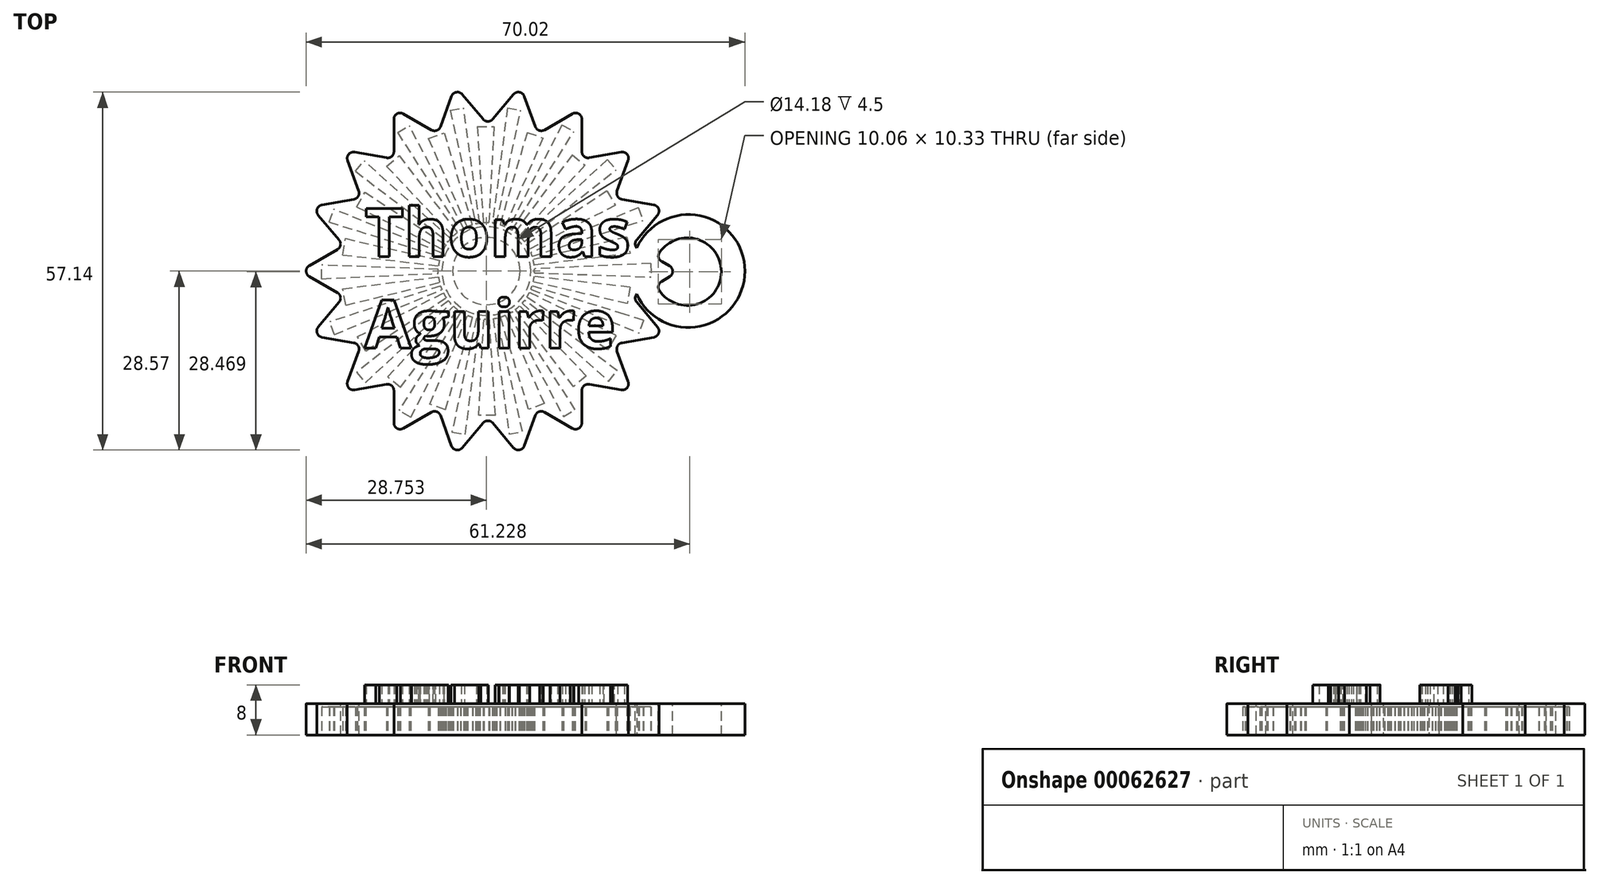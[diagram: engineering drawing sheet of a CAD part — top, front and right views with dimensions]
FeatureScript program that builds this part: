
annotation { "Feature Type Name" : "Feature", "Feature Type Description" : "" }
export const myFeature = defineFeature(function(context is Context, id is Id, definition is map)
    precondition{}
    {
        {
            var Q0;
            Q0=qCreatedBy(makeId("Top.planeOp"),FACE);
            var sketch = newSketch(context, id + "F0", { "sketchPlane" : qUnion([Q0])});
            skLineSegment(sketch, "E0", {"start": v(-64.22, 4.05) * mm, "end": v(-69.43, 10.26) * mm});
            skLineSegment(sketch, "E1", {"start": v(-69.43, 10.26) * mm, "end": v(-61.45, 11.67) * mm});
            skCircle(sketch, "E2.0", {"center": v(-41.24, 0) * mm, "radius": 30 * mm, "construction": true});
            skLineSegment(sketch, "E3", {"start": v(-61.45, 11.67) * mm, "end": v(-64.22, 19.28) * mm});
            skLineSegment(sketch, "E4", {"start": v(-64.22, 19.28) * mm, "end": v(-56.24, 17.88) * mm});
            skLineSegment(sketch, "E5", {"start": v(-56.24, 17.88) * mm, "end": v(-56.24, 25.98) * mm});
            skLineSegment(sketch, "E6", {"start": v(-56.24, 25.98) * mm, "end": v(-49.22, 21.93) * mm});
            skLineSegment(sketch, "E7", {"start": v(-49.22, 21.93) * mm, "end": v(-46.45, 29.54) * mm});
            skLineSegment(sketch, "E8", {"start": v(-46.45, 29.54) * mm, "end": v(-41.24, 23.34) * mm});
            skLineSegment(sketch, "E9", {"start": v(-41.24, 23.34) * mm, "end": v(-36.03, 29.54) * mm});
            skLineSegment(sketch, "E10", {"start": v(-36.03, 29.54) * mm, "end": v(-33.26, 21.93) * mm});
            skLineSegment(sketch, "E11", {"start": v(-33.26, 21.93) * mm, "end": v(-26.24, 25.98) * mm});
            skLineSegment(sketch, "E12", {"start": v(-26.24, 25.98) * mm, "end": v(-26.24, 17.88) * mm});
            skLineSegment(sketch, "E13", {"start": v(-26.24, 17.88) * mm, "end": v(-18.26, 19.28) * mm});
            skLineSegment(sketch, "E14", {"start": v(-18.26, 19.28) * mm, "end": v(-21.03, 11.67) * mm});
            skLineSegment(sketch, "E15", {"start": v(-21.03, 11.67) * mm, "end": v(-13.05, 10.26) * mm});
            skLineSegment(sketch, "E16", {"start": v(-13.05, 10.26) * mm, "end": v(-18.26, 4.05) * mm});
            skLineSegment(sketch, "E17", {"start": v(-18.26, 4.05) * mm, "end": v(-11.24, 0) * mm});
            skLineSegment(sketch, "E18", {"start": v(-11.24, 0) * mm, "end": v(-18.26, -4.05) * mm});
            skLineSegment(sketch, "E19", {"start": v(-18.26, -4.05) * mm, "end": v(-13.05, -10.26) * mm});
            skLineSegment(sketch, "E20", {"start": v(-13.05, -10.26) * mm, "end": v(-21.03, -11.67) * mm});
            skLineSegment(sketch, "E21", {"start": v(-21.03, -11.67) * mm, "end": v(-18.26, -19.28) * mm});
            skLineSegment(sketch, "E22", {"start": v(-18.26, -19.28) * mm, "end": v(-26.24, -17.88) * mm});
            skLineSegment(sketch, "E23", {"start": v(-26.24, -17.88) * mm, "end": v(-26.24, -25.98) * mm});
            skLineSegment(sketch, "E24", {"start": v(-26.24, -25.98) * mm, "end": v(-33.26, -21.93) * mm});
            skLineSegment(sketch, "E25", {"start": v(-33.26, -21.93) * mm, "end": v(-36.03, -29.54) * mm});
            skLineSegment(sketch, "E26", {"start": v(-46.45, -29.54) * mm, "end": v(-49.22, -21.93) * mm});
            skLineSegment(sketch, "E27", {"start": v(-49.22, -21.93) * mm, "end": v(-56.24, -25.98) * mm});
            skLineSegment(sketch, "E28", {"start": v(-56.24, -25.98) * mm, "end": v(-56.24, -17.88) * mm});
            skLineSegment(sketch, "E29", {"start": v(-56.24, -17.88) * mm, "end": v(-64.22, -19.28) * mm});
            skLineSegment(sketch, "E30", {"start": v(-64.22, -19.28) * mm, "end": v(-61.45, -11.67) * mm});
            skLineSegment(sketch, "E31", {"start": v(-61.45, -11.67) * mm, "end": v(-69.43, -10.26) * mm});
            skLineSegment(sketch, "E32", {"start": v(-69.43, -10.26) * mm, "end": v(-64.22, -4.05) * mm});
            skLineSegment(sketch, "E33", {"start": v(-64.22, -4.05) * mm, "end": v(-71.24, 0) * mm});
            skLineSegment(sketch, "E34", {"start": v(-71.24, 0) * mm, "end": v(-64.22, 4.05) * mm});
            skLineSegment(sketch, "E35", {"start": v(-46.45, -29.54) * mm, "end": v(-41.24, -23.34) * mm});
            skLineSegment(sketch, "E36", {"start": v(-41.24, -23.34) * mm, "end": v(-36.03, -29.54) * mm});
            skSolve(sketch);
        }
        {
            var Q0;
            Q0=qSketchRegion(id+"F0",true);
            extrude(context, id + "F1", {"entities" : qUnion([Q0]), "depth" : 5 * mm});
        }
        {
            var Q0;
            Q0=makeQuery(id+"F1.opExtrude","SWEPT_EDGE",EDGE,{"disambiguationData":[OSD([sQuery(id+"F0.wireOp",EDGE,"E26"),sQuery(id+"F0.wireOp",EDGE,"E27")])]});
            var Q1;
            Q1=makeQuery(id+"F1.opExtrude","SWEPT_EDGE",EDGE,{"disambiguationData":[OSD([sQuery(id+"F0.wireOp",EDGE,"E28"),sQuery(id+"F0.wireOp",EDGE,"E29")])]});
            var Q2;
            Q2=makeQuery(id+"F1.opExtrude","SWEPT_EDGE",EDGE,{"disambiguationData":[OSD([sQuery(id+"F0.wireOp",EDGE,"E30"),sQuery(id+"F0.wireOp",EDGE,"E31")])]});
            var Q3;
            Q3=makeQuery(id+"F1.opExtrude","SWEPT_EDGE",EDGE,{"disambiguationData":[OSD([sQuery(id+"F0.wireOp",EDGE,"E32"),sQuery(id+"F0.wireOp",EDGE,"E33")])]});
            var Q4;
            Q4=makeQuery(id+"F1.opExtrude","SWEPT_EDGE",EDGE,{"disambiguationData":[OSD([sQuery(id+"F0.wireOp",EDGE,"E0"),sQuery(id+"F0.wireOp",EDGE,"E34")])]});
            var Q5;
            Q5=makeQuery(id+"F1.opExtrude","SWEPT_EDGE",EDGE,{"disambiguationData":[OSD([sQuery(id+"F0.wireOp",EDGE,"E1"),sQuery(id+"F0.wireOp",EDGE,"E3")])]});
            var Q6;
            Q6=makeQuery(id+"F1.opExtrude","SWEPT_EDGE",EDGE,{"disambiguationData":[OSD([sQuery(id+"F0.wireOp",EDGE,"E4"),sQuery(id+"F0.wireOp",EDGE,"E5")])]});
            var Q7;
            Q7=makeQuery(id+"F1.opExtrude","SWEPT_EDGE",EDGE,{"disambiguationData":[OSD([sQuery(id+"F0.wireOp",EDGE,"E6"),sQuery(id+"F0.wireOp",EDGE,"E7")])]});
            var Q8;
            Q8=makeQuery(id+"F1.opExtrude","SWEPT_EDGE",EDGE,{"disambiguationData":[OSD([sQuery(id+"F0.wireOp",EDGE,"E8"),sQuery(id+"F0.wireOp",EDGE,"E9")])]});
            var Q9;
            Q9=makeQuery(id+"F1.opExtrude","SWEPT_EDGE",EDGE,{"disambiguationData":[OSD([sQuery(id+"F0.wireOp",EDGE,"E10"),sQuery(id+"F0.wireOp",EDGE,"E11")])]});
            var Q10;
            Q10=makeQuery(id+"F1.opExtrude","SWEPT_EDGE",EDGE,{"disambiguationData":[OSD([sQuery(id+"F0.wireOp",EDGE,"E35"),sQuery(id+"F0.wireOp",EDGE,"E36")])]});
            var Q11;
            Q11=makeQuery(id+"F1.opExtrude","SWEPT_EDGE",EDGE,{"disambiguationData":[OSD([sQuery(id+"F0.wireOp",EDGE,"E24"),sQuery(id+"F0.wireOp",EDGE,"E25")])]});
            var Q12;
            Q12=makeQuery(id+"F1.opExtrude","SWEPT_EDGE",EDGE,{"disambiguationData":[OSD([sQuery(id+"F0.wireOp",EDGE,"E22"),sQuery(id+"F0.wireOp",EDGE,"E23")])]});
            var Q13;
            Q13=makeQuery(id+"F1.opExtrude","SWEPT_EDGE",EDGE,{"disambiguationData":[OSD([sQuery(id+"F0.wireOp",EDGE,"E20"),sQuery(id+"F0.wireOp",EDGE,"E21")])]});
            var Q14;
            Q14=makeQuery(id+"F1.opExtrude","SWEPT_EDGE",EDGE,{"disambiguationData":[OSD([sQuery(id+"F0.wireOp",EDGE,"E12"),sQuery(id+"F0.wireOp",EDGE,"E13")])]});
            var Q15;
            Q15=makeQuery(id+"F1.opExtrude","SWEPT_EDGE",EDGE,{"disambiguationData":[OSD([sQuery(id+"F0.wireOp",EDGE,"E14"),sQuery(id+"F0.wireOp",EDGE,"E15")])]});
            var Q16;
            Q16=makeQuery(id+"F1.opExtrude","SWEPT_EDGE",EDGE,{"disambiguationData":[OSD([sQuery(id+"F0.wireOp",EDGE,"E16"),sQuery(id+"F0.wireOp",EDGE,"E17")])]});
            var Q17;
            Q17=makeQuery(id+"F1.opExtrude","SWEPT_EDGE",EDGE,{"disambiguationData":[OSD([sQuery(id+"F0.wireOp",EDGE,"E18"),sQuery(id+"F0.wireOp",EDGE,"E19")])]});
            fillet(context, id + "F2", {"entities" : qUnion([Q0, Q1, Q2, Q3, Q4, Q5, Q6, Q7, Q8, Q9, Q10, Q11, Q12, Q13, Q14, Q15, Q16, Q17]), "radius" : 1 * mm, "tangentPropagation" : true, "allowEdgeOverflow" : false});
        }
        {
            var Q0;
            Q0=makeQuery(id+"F1.opExtrude","SWEPT_EDGE",EDGE,{"disambiguationData":[OSD([sQuery(id+"F0.wireOp",EDGE,"E9"),sQuery(id+"F0.wireOp",EDGE,"E10")])]});
            var Q1;
            Q1=makeQuery(id+"F1.opExtrude","SWEPT_EDGE",EDGE,{"disambiguationData":[OSD([sQuery(id+"F0.wireOp",EDGE,"E11"),sQuery(id+"F0.wireOp",EDGE,"E12")])]});
            var Q2;
            Q2=makeQuery(id+"F1.opExtrude","SWEPT_EDGE",EDGE,{"disambiguationData":[OSD([sQuery(id+"F0.wireOp",EDGE,"E13"),sQuery(id+"F0.wireOp",EDGE,"E14")])]});
            var Q3;
            Q3=makeQuery(id+"F1.opExtrude","SWEPT_EDGE",EDGE,{"disambiguationData":[OSD([sQuery(id+"F0.wireOp",EDGE,"E15"),sQuery(id+"F0.wireOp",EDGE,"E16")])]});
            var Q4;
            Q4=makeQuery(id+"F1.opExtrude","SWEPT_EDGE",EDGE,{"disambiguationData":[OSD([sQuery(id+"F0.wireOp",EDGE,"E17"),sQuery(id+"F0.wireOp",EDGE,"E18")])]});
            var Q5;
            Q5=makeQuery(id+"F1.opExtrude","SWEPT_EDGE",EDGE,{"disambiguationData":[OSD([sQuery(id+"F0.wireOp",EDGE,"E19"),sQuery(id+"F0.wireOp",EDGE,"E20")])]});
            var Q6;
            Q6=makeQuery(id+"F1.opExtrude","SWEPT_EDGE",EDGE,{"disambiguationData":[OSD([sQuery(id+"F0.wireOp",EDGE,"E5"),sQuery(id+"F0.wireOp",EDGE,"E6")])]});
            var Q7;
            Q7=makeQuery(id+"F1.opExtrude","SWEPT_EDGE",EDGE,{"disambiguationData":[OSD([sQuery(id+"F0.wireOp",EDGE,"E7"),sQuery(id+"F0.wireOp",EDGE,"E8")])]});
            var Q8;
            Q8=makeQuery(id+"F1.opExtrude","SWEPT_EDGE",EDGE,{"disambiguationData":[OSD([sQuery(id+"F0.wireOp",EDGE,"E3"),sQuery(id+"F0.wireOp",EDGE,"E4")])]});
            var Q9;
            Q9=makeQuery(id+"F1.opExtrude","SWEPT_EDGE",EDGE,{"disambiguationData":[OSD([sQuery(id+"F0.wireOp",EDGE,"E0"),sQuery(id+"F0.wireOp",EDGE,"E1")])]});
            var Q10;
            Q10=makeQuery(id+"F1.opExtrude","SWEPT_EDGE",EDGE,{"disambiguationData":[OSD([sQuery(id+"F0.wireOp",EDGE,"E33"),sQuery(id+"F0.wireOp",EDGE,"E34")])]});
            var Q11;
            Q11=makeQuery(id+"F1.opExtrude","SWEPT_EDGE",EDGE,{"disambiguationData":[OSD([sQuery(id+"F0.wireOp",EDGE,"E31"),sQuery(id+"F0.wireOp",EDGE,"E32")])]});
            var Q12;
            Q12=makeQuery(id+"F1.opExtrude","SWEPT_EDGE",EDGE,{"disambiguationData":[OSD([sQuery(id+"F0.wireOp",EDGE,"E29"),sQuery(id+"F0.wireOp",EDGE,"E30")])]});
            var Q13;
            Q13=makeQuery(id+"F1.opExtrude","SWEPT_EDGE",EDGE,{"disambiguationData":[OSD([sQuery(id+"F0.wireOp",EDGE,"E27"),sQuery(id+"F0.wireOp",EDGE,"E28")])]});
            var Q14;
            Q14=makeQuery(id+"F1.opExtrude","SWEPT_EDGE",EDGE,{"disambiguationData":[OSD([sQuery(id+"F0.wireOp",EDGE,"E26"),sQuery(id+"F0.wireOp",EDGE,"E35")])]});
            var Q15;
            Q15=makeQuery(id+"F1.opExtrude","SWEPT_EDGE",EDGE,{"disambiguationData":[OSD([sQuery(id+"F0.wireOp",EDGE,"E25"),sQuery(id+"F0.wireOp",EDGE,"E36")])]});
            var Q16;
            Q16=makeQuery(id+"F1.opExtrude","SWEPT_EDGE",EDGE,{"disambiguationData":[OSD([sQuery(id+"F0.wireOp",EDGE,"E23"),sQuery(id+"F0.wireOp",EDGE,"E24")])]});
            var Q17;
            Q17=makeQuery(id+"F1.opExtrude","SWEPT_EDGE",EDGE,{"disambiguationData":[OSD([sQuery(id+"F0.wireOp",EDGE,"E21"),sQuery(id+"F0.wireOp",EDGE,"E22")])]});
            fillet(context, id + "F3", {"entities" : qUnion([Q0, Q1, Q2, Q3, Q4, Q5, Q6, Q7, Q8, Q9, Q10, Q11, Q12, Q13, Q14, Q15, Q16, Q17]), "radius" : 1 * mm, "tangentPropagation" : true, "allowEdgeOverflow" : false});
        }
        {
            var Q0;
            Q0=qCreatedBy(makeId("Top.planeOp"),FACE);
            var sketch = newSketch(context, id + "F4", { "sketchPlane" : qUnion([Q0])});
            skCircle(sketch, "E37", {"center": v(-9.24, 0) * mm, "radius": 9.02 * mm});
            skSolve(sketch);
        }
        {
            var Q0;
            Q0=qSketchRegion(id+"F4",true);
            var Q1;
            {var subQ0=sQuery(id+"F0.wireOp",EDGE,"E30");var subQ1=sQuery(id+"F0.wireOp",EDGE,"E16");var subQ2=sQuery(id+"F0.wireOp",EDGE,"E31");var subQ3=sQuery(id+"F0.wireOp",EDGE,"E27");var subQ4=sQuery(id+"F0.wireOp",EDGE,"E23");var subQ5=sQuery(id+"F0.wireOp",EDGE,"E21");var subQ6=sQuery(id+"F0.wireOp",EDGE,"E13");var subQ7=sQuery(id+"F0.wireOp",EDGE,"E14");var subQ8=sQuery(id+"F0.wireOp",EDGE,"E20");var subQ9=sQuery(id+"F0.wireOp",EDGE,"E22");var subQ10=sQuery(id+"F0.wireOp",EDGE,"E19");var subQ11=sQuery(id+"F0.wireOp",EDGE,"E11");var subQ12=sQuery(id+"F0.wireOp",EDGE,"E18");var subQ13=sQuery(id+"F0.wireOp",EDGE,"E17");var subQ14=sQuery(id+"F0.wireOp",EDGE,"E12");var subQ15=sQuery(id+"F0.wireOp",EDGE,"E4");var subQ16=sQuery(id+"F0.wireOp",EDGE,"E3");var subQ17=sQuery(id+"F0.wireOp",EDGE,"E32");var subQ18=sQuery(id+"F0.wireOp",EDGE,"E1");var subQ19=sQuery(id+"F0.wireOp",EDGE,"E9");var subQ20=sQuery(id+"F0.wireOp",EDGE,"E0");var subQ21=sQuery(id+"F0.wireOp",EDGE,"E5");var subQ22=sQuery(id+"F0.wireOp",EDGE,"E6");var subQ23=sQuery(id+"F0.wireOp",EDGE,"E7");var subQ24=sQuery(id+"F0.wireOp",EDGE,"E36");var subQ25=sQuery(id+"F0.wireOp",EDGE,"E15");var subQ26=sQuery(id+"F0.wireOp",EDGE,"E8");var subQ27=sQuery(id+"F0.wireOp",EDGE,"E34");var subQ28=sQuery(id+"F0.wireOp",EDGE,"E25");var subQ29=sQuery(id+"F0.wireOp",EDGE,"E29");var subQ30=sQuery(id+"F0.wireOp",EDGE,"E26");var subQ31=sQuery(id+"F0.wireOp",EDGE,"E35");var subQ32=sQuery(id+"F0.wireOp",EDGE,"E33");var subQ33=sQuery(id+"F0.wireOp",EDGE,"E24");var subQ34=sQuery(id+"F0.wireOp",EDGE,"E10");var subQ35=sQuery(id+"F0.wireOp",EDGE,"E28");Q1=makeQuery(id+"FIdaEZY0NoQjCEp_1.boolean.opBoolean","SPLIT",FACE,{"disambiguationData":[TD([makeQuery(id+"F1.opExtrude","SWEPT_FACE",FACE,{"disambiguationData":[OSD([subQ20])]})])],"derivedFrom":makeQuery(id+"F1.opExtrude","CAP_FACE",FACE,{"disambiguationData":[OSD([subQ20,subQ18,subQ16,subQ15,subQ21,subQ22,subQ23,subQ26,subQ19,subQ34,subQ11,subQ14,subQ6,subQ7,subQ25,subQ1,subQ13,subQ12,subQ10,subQ8,subQ5,subQ9,subQ4,subQ33,subQ28,subQ30,subQ3,subQ35,subQ29,subQ0,subQ2,subQ17,subQ32,subQ27,subQ31,subQ24])],"isStart":false})});}
            extrude(context, id + "F5", {"entities" : qUnion([Q0]), "operationType" : NewBodyOperationType.ADD, "endBound" : BoundingType.UP_TO_SURFACE, "endBoundEntityFace" : qUnion([Q1]), "depth" : 25 * mm});
        }
        {
            var Q0;
            {var subQ0=sQuery(id+"F0.wireOp",EDGE,"E36");var subQ1=sQuery(id+"F0.wireOp",EDGE,"E35");var subQ2=sQuery(id+"F0.wireOp",EDGE,"E34");var subQ3=sQuery(id+"F0.wireOp",EDGE,"E33");var subQ4=sQuery(id+"F0.wireOp",EDGE,"E32");var subQ5=sQuery(id+"F0.wireOp",EDGE,"E31");var subQ6=sQuery(id+"F0.wireOp",EDGE,"E30");var subQ7=sQuery(id+"F0.wireOp",EDGE,"E29");var subQ8=sQuery(id+"F0.wireOp",EDGE,"E28");var subQ9=sQuery(id+"F0.wireOp",EDGE,"E27");var subQ10=sQuery(id+"F0.wireOp",EDGE,"E26");var subQ11=sQuery(id+"F0.wireOp",EDGE,"E25");var subQ12=sQuery(id+"F0.wireOp",EDGE,"E24");var subQ13=sQuery(id+"F0.wireOp",EDGE,"E23");var subQ14=sQuery(id+"F0.wireOp",EDGE,"E22");var subQ15=sQuery(id+"F0.wireOp",EDGE,"E21");var subQ16=sQuery(id+"F0.wireOp",EDGE,"E20");var subQ17=sQuery(id+"F0.wireOp",EDGE,"E19");var subQ18=sQuery(id+"F0.wireOp",EDGE,"E18");var subQ19=sQuery(id+"F0.wireOp",EDGE,"E17");var subQ20=sQuery(id+"F0.wireOp",EDGE,"E16");var subQ21=sQuery(id+"F0.wireOp",EDGE,"E15");var subQ22=sQuery(id+"F0.wireOp",EDGE,"E14");var subQ23=sQuery(id+"F0.wireOp",EDGE,"E13");var subQ24=sQuery(id+"F0.wireOp",EDGE,"E12");var subQ25=sQuery(id+"F0.wireOp",EDGE,"E11");var subQ26=sQuery(id+"F0.wireOp",EDGE,"E10");var subQ27=sQuery(id+"F0.wireOp",EDGE,"E9");var subQ28=sQuery(id+"F0.wireOp",EDGE,"E8");var subQ29=sQuery(id+"F0.wireOp",EDGE,"E7");var subQ30=sQuery(id+"F0.wireOp",EDGE,"E6");var subQ31=sQuery(id+"F0.wireOp",EDGE,"E5");var subQ32=sQuery(id+"F0.wireOp",EDGE,"E4");var subQ33=sQuery(id+"F0.wireOp",EDGE,"E3");var subQ34=sQuery(id+"F0.wireOp",EDGE,"E1");var subQ35=sQuery(id+"F0.wireOp",EDGE,"E0");Q0=makeQuery(id+"F5.boolean.opBoolean","MERGE",FACE,{"derivedFrom":[makeQuery(id+"F1.opExtrude","CAP_FACE",FACE,{"disambiguationData":[OSD([subQ35,subQ34,subQ33,subQ32,subQ31,subQ30,subQ29,subQ28,subQ27,subQ26,subQ25,subQ24,subQ23,subQ22,subQ21,subQ20,subQ19,subQ18,subQ17,subQ16,subQ15,subQ14,subQ13,subQ12,subQ11,subQ10,subQ9,subQ8,subQ7,subQ6,subQ5,subQ4,subQ3,subQ2,subQ1,subQ0])],"isStart":false}),makeQuery(id+"F5.opExtrude","CAP_FACE",FACE,{"disambiguationData":[OSD([subQ35,subQ34,subQ33,subQ32,subQ31,subQ30,subQ29,subQ28,subQ27,subQ26,subQ25,subQ24,subQ23,subQ22,subQ21,subQ20,subQ19,subQ18,subQ17,subQ16,subQ15,subQ14,subQ13,subQ12,subQ11,subQ10,subQ9,subQ8,subQ7,subQ6,subQ5,subQ4,subQ3,subQ2,subQ1,subQ0])],"isStart":false})]});}
            var sketch = newSketch(context, id + "F6", { "sketchPlane" : qUnion([Q0])});
            skLineSegment(sketch, "E38", {"start": v(-14.37, 2) * mm, "end": v(-10.75, 0) * mm});
            skLineSegment(sketch, "E39", {"start": v(-10.75, 0) * mm, "end": v(-14.37, -2.19) * mm});
            skArc(sketch, "E40", {"start": v(-14.37, -2.19) * mm, "mid": v(-3.98, -0.1) * mm, "end": v(-14.37, 2) * mm});
            skSolve(sketch);
        }
        {
            var Q0;
            Q0=qSketchRegion(id+"F6",true);
            var Q1;
            Q1=makeQuery(id+"F5.boolean.opBoolean","MERGE",FACE,{"derivedFrom":[makeQuery(id+"F1.opExtrude","CAP_FACE",FACE,{"disambiguationData":[OSD([sQuery(id+"F0.wireOp",EDGE,"E0"),sQuery(id+"F0.wireOp",EDGE,"E1"),sQuery(id+"F0.wireOp",EDGE,"E3"),sQuery(id+"F0.wireOp",EDGE,"E4"),sQuery(id+"F0.wireOp",EDGE,"E5"),sQuery(id+"F0.wireOp",EDGE,"E6"),sQuery(id+"F0.wireOp",EDGE,"E7"),sQuery(id+"F0.wireOp",EDGE,"E8"),sQuery(id+"F0.wireOp",EDGE,"E9"),sQuery(id+"F0.wireOp",EDGE,"E10"),sQuery(id+"F0.wireOp",EDGE,"E11"),sQuery(id+"F0.wireOp",EDGE,"E12"),sQuery(id+"F0.wireOp",EDGE,"E13"),sQuery(id+"F0.wireOp",EDGE,"E14"),sQuery(id+"F0.wireOp",EDGE,"E15"),sQuery(id+"F0.wireOp",EDGE,"E16"),sQuery(id+"F0.wireOp",EDGE,"E17"),sQuery(id+"F0.wireOp",EDGE,"E18"),sQuery(id+"F0.wireOp",EDGE,"E19"),sQuery(id+"F0.wireOp",EDGE,"E20"),sQuery(id+"F0.wireOp",EDGE,"E21"),sQuery(id+"F0.wireOp",EDGE,"E22"),sQuery(id+"F0.wireOp",EDGE,"E23"),sQuery(id+"F0.wireOp",EDGE,"E24"),sQuery(id+"F0.wireOp",EDGE,"E25"),sQuery(id+"F0.wireOp",EDGE,"E26"),sQuery(id+"F0.wireOp",EDGE,"E27"),sQuery(id+"F0.wireOp",EDGE,"E28"),sQuery(id+"F0.wireOp",EDGE,"E29"),sQuery(id+"F0.wireOp",EDGE,"E30"),sQuery(id+"F0.wireOp",EDGE,"E31"),sQuery(id+"F0.wireOp",EDGE,"E32"),sQuery(id+"F0.wireOp",EDGE,"E33"),sQuery(id+"F0.wireOp",EDGE,"E34"),sQuery(id+"F0.wireOp",EDGE,"E35"),sQuery(id+"F0.wireOp",EDGE,"E36")])],"isStart":true}),makeQuery(id+"F5.opExtrude","CAP_FACE",FACE,{"disambiguationData":[OSD([sQuery(id+"F4.wireOp",EDGE,"E37")])],"isStart":true})]});
            extrude(context, id + "F7", {"entities" : qUnion([Q0]), "operationType" : NewBodyOperationType.REMOVE, "endBound" : BoundingType.UP_TO_SURFACE, "oppositeDirection" : true, "endBoundEntityFace" : qUnion([Q1]), "depth" : 25 * mm});
        }
        {
            var Q0;
            Q0=makeQuery(id+"F7.boolean.opBoolean","COPY",EDGE,{"derivedFrom":makeQuery(id+"F7.opExtrude","SWEPT_EDGE",EDGE,{"disambiguationData":[OSD([sQuery(id+"F6.wireOp",EDGE,"KMGjyx1H-Efwy-Ger7-KHIj-FZDtgPy88TKw"),sQuery(id+"F6.wireOp",EDGE,"Em1Z4o3I-NRpS-VtHU-MFej-VVcVSapDzxZl")])]})});
            var Q1;
            Q1=makeQuery(id+"F7.boolean.opBoolean","COPY",EDGE,{"derivedFrom":makeQuery(id+"F7.opExtrude","SWEPT_EDGE",EDGE,{"disambiguationData":[OSD([sQuery(id+"F6.wireOp",EDGE,"E38"),sQuery(id+"F6.wireOp",EDGE,"E39")])]})});
            var Q2;
            Q2=makeQuery(id+"F7.boolean.opBoolean","COPY",EDGE,{"derivedFrom":makeQuery(id+"F7.opExtrude","SWEPT_EDGE",EDGE,{"disambiguationData":[OSD([sQuery(id+"F6.wireOp",EDGE,"E39"),sQuery(id+"F6.wireOp",EDGE,"E40")])]})});
            var Q3;
            Q3=makeQuery(id+"F7.boolean.opBoolean","COPY",EDGE,{"derivedFrom":makeQuery(id+"F7.opExtrude","SWEPT_EDGE",EDGE,{"disambiguationData":[OSD([sQuery(id+"F6.wireOp",EDGE,"E38"),sQuery(id+"F6.wireOp",EDGE,"E40")])]})});
            fillet(context, id + "F8", {"entities" : qUnion([Q0, Q1, Q2, Q3]), "radius" : 1 * mm, "tangentPropagation" : true, "allowEdgeOverflow" : false});
        }
        {
            var Q0;
            Q0=makeQuery(id+"F0.imprint","IMPRINT",FACE,{"disambiguationData":[TD([[makeQuery(id+"F0.imprint","IMPRINT",EDGE,{"derivedFrom":sQuery(id+"F0.wireOp",EDGE,"E0")}),-1.0]])]});
            var sketch = newSketch(context, id + "F9", { "sketchPlane" : qUnion([Q0])});
            skCircle(sketch, "E41", {"center": v(-41.49, 0) * mm, "radius": 26.28 * mm, "construction": true});
            skCircle(sketch, "E42", {"center": v(-41.49, 0) * mm, "radius": 23.08 * mm, "construction": true});
            skLineSegment(sketch, "E43", {"start": v(-41.49, 0) * mm, "end": v(-21.98, -17.6) * mm, "construction": true});
            skLineSegment(sketch, "E44", {"start": v(-21.98, -17.6) * mm, "end": v(-20.6, -15.94) * mm, "construction": true});
            skLineSegment(sketch, "E45", {"start": v(-20.6, -15.94) * mm, "end": v(-41.49, 0) * mm, "construction": true});
            skLineSegment(sketch, "E46", {"start": v(-41.49, 0) * mm, "end": v(-22.13, -12.57) * mm, "construction": true});
            skLineSegment(sketch, "E47", {"start": v(-22.13, -12.57) * mm, "end": v(-20.8, -10.26) * mm, "construction": true});
            skLineSegment(sketch, "E48", {"start": v(-20.8, -10.26) * mm, "end": v(-41.49, 0) * mm, "construction": true});
            skLineSegment(sketch, "E49", {"start": v(-41.49, 0) * mm, "end": v(-21.03, -11.67) * mm, "construction": true});
            skLineSegment(sketch, "E50", {"start": v(-41.49, 0) * mm, "end": v(-18.26, -19.28) * mm, "construction": true});
            skLineSegment(sketch, "E51", {"start": v(-20.8, -10.26) * mm, "end": v(-21.03, -11.67) * mm, "construction": true});
            skLineSegment(sketch, "E52", {"start": v(-22.13, -12.57) * mm, "end": v(-21.03, -11.67) * mm, "construction": true});
            skLineSegment(sketch, "E53", {"start": v(-18.26, -19.28) * mm, "end": v(-21.98, -17.6) * mm, "construction": true});
            skLineSegment(sketch, "E54", {"start": v(-20.6, -15.94) * mm, "end": v(-18.26, -19.28) * mm, "construction": true});
            skLineSegment(sketch, "E55", {"start": v(-35.78, -5.15) * mm, "end": v(-21.98, -17.6) * mm});
            skLineSegment(sketch, "E56", {"start": v(-20.6, -15.94) * mm, "end": v(-35.38, -4.66) * mm});
            skLineSegment(sketch, "E57", {"start": v(-22.13, -12.57) * mm, "end": v(-35.04, -4.18) * mm});
            skLineSegment(sketch, "E58", {"start": v(-20.8, -10.26) * mm, "end": v(-22.13, -12.57) * mm});
            skLineSegment(sketch, "E59", {"start": v(-20.8, -10.26) * mm, "end": v(-34.6, -3.42) * mm});
            skLineSegment(sketch, "E60.1.0", {"start": v(-34.37, -2.89) * mm, "end": v(-17.13, -9.87) * mm});
            skLineSegment(sketch, "E60.1.1", {"start": v(-17.13, -9.87) * mm, "end": v(-16.4, -7.83) * mm, "construction": true});
            skLineSegment(sketch, "E60.1.2", {"start": v(-16.4, -7.83) * mm, "end": v(-19.45, -6.88) * mm});
            skLineSegment(sketch, "E60.1.3", {"start": v(-19, -5.2) * mm, "end": v(-34, -1.73) * mm});
            skLineSegment(sketch, "E60.1.4", {"start": v(-18.55, -2.57) * mm, "end": v(-19, -5.2) * mm});
            skLineSegment(sketch, "E60.1.5", {"start": v(-18.55, -2.57) * mm, "end": v(-33.85, -0.86) * mm});
            skLineSegment(sketch, "E60.2.0", {"start": v(-33.8, -0.28) * mm, "end": v(-15.22, -0.95) * mm});
            skLineSegment(sketch, "E60.2.1", {"start": v(-15.22, -0.95) * mm, "end": v(-15.23, 1.22) * mm, "construction": true});
            skLineSegment(sketch, "E60.2.2", {"start": v(-15.23, 1.22) * mm, "end": v(-33.81, 0.36) * mm});
            skLineSegment(sketch, "E60.2.3", {"start": v(-18.57, 2.81) * mm, "end": v(-33.86, 0.94) * mm});
            skLineSegment(sketch, "E60.2.4", {"start": v(-19.05, 5.43) * mm, "end": v(-18.57, 2.81) * mm});
            skLineSegment(sketch, "E60.2.5", {"start": v(-19.05, 5.43) * mm, "end": v(-34.02, 1.8) * mm});
            skLineSegment(sketch, "E60.3.0", {"start": v(-34.18, 2.37) * mm, "end": v(-16.48, 8.1) * mm});
            skLineSegment(sketch, "E60.3.1", {"start": v(-16.48, 8.1) * mm, "end": v(-17.23, 10.13) * mm, "construction": true});
            skLineSegment(sketch, "E60.3.2", {"start": v(-17.23, 10.13) * mm, "end": v(-34.4, 2.96) * mm});
            skLineSegment(sketch, "E60.3.3", {"start": v(-20.92, 10.48) * mm, "end": v(-34.64, 3.49) * mm});
            skLineSegment(sketch, "E60.3.4", {"start": v(-22.26, 12.78) * mm, "end": v(-20.92, 10.48) * mm});
            skLineSegment(sketch, "E60.3.5", {"start": v(-22.26, 12.78) * mm, "end": v(-35.09, 4.25) * mm});
            skLineSegment(sketch, "E60.4.0", {"start": v(-35.43, 4.72) * mm, "end": v(-20.76, 16.16) * mm});
            skLineSegment(sketch, "E60.4.1", {"start": v(-20.76, 16.16) * mm, "end": v(-22.16, 17.81) * mm, "construction": true});
            skLineSegment(sketch, "E60.4.2", {"start": v(-22.16, 17.81) * mm, "end": v(-35.84, 5.2) * mm});
            skLineSegment(sketch, "E60.4.3", {"start": v(-25.74, 16.88) * mm, "end": v(-36.25, 5.62) * mm});
            skLineSegment(sketch, "E60.4.4", {"start": v(-27.79, 18.58) * mm, "end": v(-25.74, 16.88) * mm});
            skLineSegment(sketch, "E60.4.5", {"start": v(-27.79, 18.58) * mm, "end": v(-36.93, 6.18) * mm});
            skLineSegment(sketch, "E60.5.0", {"start": v(-37.4, 6.51) * mm, "end": v(-27.53, 22.27) * mm});
            skLineSegment(sketch, "E60.5.1", {"start": v(-27.53, 22.27) * mm, "end": v(-29.42, 23.35) * mm, "construction": true});
            skLineSegment(sketch, "E60.5.2", {"start": v(-29.42, 23.35) * mm, "end": v(-37.96, 6.83) * mm});
            skLineSegment(sketch, "E60.5.3", {"start": v(-32.47, 21.25) * mm, "end": v(-38.48, 7.07) * mm});
            skLineSegment(sketch, "E60.5.4", {"start": v(-34.97, 22.15) * mm, "end": v(-32.47, 21.25) * mm});
            skLineSegment(sketch, "E60.5.5", {"start": v(-34.97, 22.15) * mm, "end": v(-39.32, 7.37) * mm});
            skLineSegment(sketch, "E60.6.0", {"start": v(-39.88, 7.51) * mm, "end": v(-36, 25.7) * mm});
            skLineSegment(sketch, "E60.6.1", {"start": v(-36, 25.7) * mm, "end": v(-38.13, 26.07) * mm, "construction": true});
            skLineSegment(sketch, "E60.6.2", {"start": v(-38.13, 26.07) * mm, "end": v(-40.5, 7.62) * mm});
            skLineSegment(sketch, "E60.6.3", {"start": v(-40.28, 23.05) * mm, "end": v(-41.08, 7.67) * mm});
            skLineSegment(sketch, "E60.6.4", {"start": v(-42.94, 23.04) * mm, "end": v(-40.28, 23.05) * mm});
            skLineSegment(sketch, "E60.6.5", {"start": v(-42.94, 23.04) * mm, "end": v(-41.97, 7.67) * mm});
            skLineSegment(sketch, "E60.7.0", {"start": v(-42.55, 7.6) * mm, "end": v(-45.11, 26.03) * mm});
            skLineSegment(sketch, "E60.7.1", {"start": v(-45.11, 26.03) * mm, "end": v(-47.25, 25.64) * mm, "construction": true});
            skLineSegment(sketch, "E60.7.2", {"start": v(-47.25, 25.64) * mm, "end": v(-43.17, 7.5) * mm});
            skLineSegment(sketch, "E60.7.3", {"start": v(-48.24, 22.08) * mm, "end": v(-43.73, 7.35) * mm});
            skLineSegment(sketch, "E60.7.4", {"start": v(-50.73, 21.15) * mm, "end": v(-48.24, 22.08) * mm});
            skLineSegment(sketch, "E60.7.5", {"start": v(-50.73, 21.15) * mm, "end": v(-44.56, 7.04) * mm});
            skLineSegment(sketch, "E60.8.0", {"start": v(-45.09, 6.79) * mm, "end": v(-53.8, 23.22) * mm});
            skLineSegment(sketch, "E60.8.1", {"start": v(-53.8, 23.22) * mm, "end": v(-55.67, 22.13) * mm, "construction": true});
            skLineSegment(sketch, "E60.8.2", {"start": v(-55.67, 22.13) * mm, "end": v(-45.63, 6.47) * mm});
            skLineSegment(sketch, "E60.8.3", {"start": v(-55.38, 18.44) * mm, "end": v(-46.11, 6.14) * mm});
            skLineSegment(sketch, "E60.8.4", {"start": v(-57.4, 16.72) * mm, "end": v(-55.38, 18.44) * mm});
            skLineSegment(sketch, "E60.8.5", {"start": v(-57.4, 16.72) * mm, "end": v(-46.79, 5.56) * mm});
            skLineSegment(sketch, "E60.9.0", {"start": v(-47.2, 5.15) * mm, "end": v(-61, 17.6) * mm});
            skLineSegment(sketch, "E60.9.1", {"start": v(-61, 17.6) * mm, "end": v(-62.38, 15.94) * mm, "construction": true});
            skLineSegment(sketch, "E60.9.2", {"start": v(-62.38, 15.94) * mm, "end": v(-47.6, 4.66) * mm});
            skLineSegment(sketch, "E60.9.3", {"start": v(-60.85, 12.57) * mm, "end": v(-47.93, 4.18) * mm});
            skLineSegment(sketch, "E60.9.4", {"start": v(-62.16, 10.26) * mm, "end": v(-60.85, 12.57) * mm});
            skLineSegment(sketch, "E60.9.5", {"start": v(-62.16, 10.26) * mm, "end": v(-48.37, 3.42) * mm});
            skLineSegment(sketch, "E60.10.0", {"start": v(-48.6, 2.89) * mm, "end": v(-65.84, 9.87) * mm});
            skLineSegment(sketch, "E60.10.1", {"start": v(-65.84, 9.87) * mm, "end": v(-66.57, 7.83) * mm, "construction": true});
            skLineSegment(sketch, "E60.10.2", {"start": v(-66.57, 7.83) * mm, "end": v(-48.82, 2.29) * mm});
            skLineSegment(sketch, "E60.10.3", {"start": v(-63.98, 5.2) * mm, "end": v(-48.97, 1.73) * mm});
            skLineSegment(sketch, "E60.10.4", {"start": v(-64.43, 2.57) * mm, "end": v(-63.98, 5.2) * mm});
            skLineSegment(sketch, "E60.10.5", {"start": v(-64.43, 2.57) * mm, "end": v(-49.12, 0.86) * mm});
            skLineSegment(sketch, "E60.11.0", {"start": v(-49.17, 0.28) * mm, "end": v(-67.75, 0.95) * mm});
            skLineSegment(sketch, "E60.11.1", {"start": v(-67.75, 0.95) * mm, "end": v(-67.74, -1.22) * mm, "construction": true});
            skLineSegment(sketch, "E60.11.2", {"start": v(-67.74, -1.22) * mm, "end": v(-49.16, -0.36) * mm});
            skLineSegment(sketch, "E60.11.3", {"start": v(-64.4, -2.81) * mm, "end": v(-49.11, -0.94) * mm});
            skLineSegment(sketch, "E60.11.4", {"start": v(-63.92, -5.43) * mm, "end": v(-64.4, -2.81) * mm});
            skLineSegment(sketch, "E60.11.5", {"start": v(-63.92, -5.43) * mm, "end": v(-48.95, -1.8) * mm});
            skLineSegment(sketch, "E60.12.0", {"start": v(-48.8, -2.37) * mm, "end": v(-66.5, -8.1) * mm});
            skLineSegment(sketch, "E60.12.1", {"start": v(-66.5, -8.1) * mm, "end": v(-65.74, -10.13) * mm, "construction": true});
            skLineSegment(sketch, "E60.12.2", {"start": v(-65.74, -10.13) * mm, "end": v(-48.58, -2.96) * mm});
            skLineSegment(sketch, "E60.12.3", {"start": v(-62.06, -10.48) * mm, "end": v(-48.33, -3.49) * mm});
            skLineSegment(sketch, "E60.12.4", {"start": v(-60.71, -12.78) * mm, "end": v(-62.06, -10.48) * mm});
            skLineSegment(sketch, "E60.12.5", {"start": v(-60.71, -12.78) * mm, "end": v(-47.89, -4.25) * mm});
            skLineSegment(sketch, "E60.13.0", {"start": v(-47.55, -4.72) * mm, "end": v(-62.22, -16.16) * mm});
            skLineSegment(sketch, "E60.13.1", {"start": v(-62.22, -16.16) * mm, "end": v(-60.81, -17.81) * mm, "construction": true});
            skLineSegment(sketch, "E60.13.2", {"start": v(-60.81, -17.81) * mm, "end": v(-47.14, -5.2) * mm});
            skLineSegment(sketch, "E60.13.3", {"start": v(-57.23, -16.88) * mm, "end": v(-46.73, -5.62) * mm});
            skLineSegment(sketch, "E60.13.4", {"start": v(-55.18, -18.58) * mm, "end": v(-57.23, -16.88) * mm});
            skLineSegment(sketch, "E60.13.5", {"start": v(-55.18, -18.58) * mm, "end": v(-46.05, -6.18) * mm});
            skLineSegment(sketch, "E60.14.0", {"start": v(-45.57, -6.51) * mm, "end": v(-55.44, -22.27) * mm});
            skLineSegment(sketch, "E60.14.1", {"start": v(-55.44, -22.27) * mm, "end": v(-53.56, -23.35) * mm, "construction": true});
            skLineSegment(sketch, "E60.14.2", {"start": v(-53.56, -23.35) * mm, "end": v(-45.01, -6.83) * mm});
            skLineSegment(sketch, "E60.14.3", {"start": v(-50.5, -21.25) * mm, "end": v(-44.49, -7.07) * mm});
            skLineSegment(sketch, "E60.14.4", {"start": v(-48, -22.15) * mm, "end": v(-50.5, -21.25) * mm});
            skLineSegment(sketch, "E60.14.5", {"start": v(-48, -22.15) * mm, "end": v(-43.66, -7.37) * mm});
            skLineSegment(sketch, "E60.15.0", {"start": v(-43.1, -7.51) * mm, "end": v(-46.98, -25.7) * mm});
            skLineSegment(sketch, "E60.15.1", {"start": v(-46.98, -25.7) * mm, "end": v(-44.84, -26.07) * mm, "construction": true});
            skLineSegment(sketch, "E60.15.2", {"start": v(-44.84, -26.07) * mm, "end": v(-42.47, -7.62) * mm});
            skLineSegment(sketch, "E60.15.3", {"start": v(-42.7, -23.05) * mm, "end": v(-41.89, -7.67) * mm});
            skLineSegment(sketch, "E60.15.4", {"start": v(-40.04, -23.04) * mm, "end": v(-42.7, -23.05) * mm});
            skLineSegment(sketch, "E60.15.5", {"start": v(-40.04, -23.04) * mm, "end": v(-41, -7.67) * mm});
            skLineSegment(sketch, "E60.16.0", {"start": v(-40.43, -7.6) * mm, "end": v(-37.86, -26.03) * mm});
            skLineSegment(sketch, "E60.16.1", {"start": v(-37.86, -26.03) * mm, "end": v(-35.73, -25.64) * mm, "construction": true});
            skLineSegment(sketch, "E60.16.2", {"start": v(-35.73, -25.64) * mm, "end": v(-39.8, -7.5) * mm});
            skLineSegment(sketch, "E60.16.3", {"start": v(-34.74, -22.08) * mm, "end": v(-39.24, -7.35) * mm});
            skLineSegment(sketch, "E60.16.4", {"start": v(-32.24, -21.15) * mm, "end": v(-34.74, -22.08) * mm});
            skLineSegment(sketch, "E60.16.5", {"start": v(-32.24, -21.15) * mm, "end": v(-38.41, -7.04) * mm});
            skLineSegment(sketch, "E60.17.0", {"start": v(-37.89, -6.79) * mm, "end": v(-29.18, -23.22) * mm});
            skLineSegment(sketch, "E60.17.1", {"start": v(-29.18, -23.22) * mm, "end": v(-27.3, -22.13) * mm, "construction": true});
            skLineSegment(sketch, "E60.17.2", {"start": v(-27.3, -22.13) * mm, "end": v(-37.34, -6.47) * mm});
            skLineSegment(sketch, "E60.17.3", {"start": v(-27.6, -18.44) * mm, "end": v(-36.86, -6.14) * mm});
            skLineSegment(sketch, "E60.17.4", {"start": v(-25.57, -16.72) * mm, "end": v(-27.6, -18.44) * mm});
            skLineSegment(sketch, "E60.17.5", {"start": v(-25.57, -16.72) * mm, "end": v(-36.19, -5.56) * mm});
            skArc(sketch, "E61", {"start": v(-45.09, 6.79) * mm, "mid": v(-45.36, 6.63) * mm, "end": v(-45.63, 6.47) * mm});
            skArc(sketch, "E62.trimOffspring", {"start": v(-46.11, 6.14) * mm, "mid": v(-46.46, 5.86) * mm, "end": v(-46.79, 5.56) * mm});
            skArc(sketch, "E63.trimOffspring", {"start": v(-47.2, 5.15) * mm, "mid": v(-47.4, 4.9) * mm, "end": v(-47.6, 4.66) * mm});
            skArc(sketch, "E64.trimOffspring", {"start": v(-47.93, 4.18) * mm, "mid": v(-48.16, 3.8) * mm, "end": v(-48.37, 3.42) * mm});
            skArc(sketch, "E65.trimOffspring", {"start": v(-48.6, 2.89) * mm, "mid": v(-48.72, 2.6) * mm, "end": v(-48.82, 2.29) * mm});
            skArc(sketch, "E66.trimOffspring", {"start": v(-48.97, 1.73) * mm, "mid": v(-49.06, 1.3) * mm, "end": v(-49.12, 0.86) * mm});
            skArc(sketch, "E67.trimOffspring", {"start": v(-43.73, 7.35) * mm, "mid": v(-44.15, 7.2) * mm, "end": v(-44.56, 7.04) * mm});
            skArc(sketch, "E68.trimOffspring", {"start": v(-42.55, 7.6) * mm, "mid": v(-42.86, 7.56) * mm, "end": v(-43.17, 7.5) * mm});
            skArc(sketch, "E69.trimOffspring", {"start": v(-41.08, 7.67) * mm, "mid": v(-41.53, 7.68) * mm, "end": v(-41.97, 7.67) * mm});
            skArc(sketch, "E70.trimOffspring", {"start": v(-39.88, 7.51) * mm, "mid": v(-40.2, 7.57) * mm, "end": v(-40.5, 7.62) * mm});
            skArc(sketch, "E71.trimOffspring", {"start": v(-38.48, 7.07) * mm, "mid": v(-38.9, 7.23) * mm, "end": v(-39.32, 7.37) * mm});
            skArc(sketch, "E72.trimOffspring", {"start": v(-37.4, 6.51) * mm, "mid": v(-37.68, 6.67) * mm, "end": v(-37.96, 6.83) * mm});
            skArc(sketch, "E73.trimOffspring", {"start": v(-36.25, 5.62) * mm, "mid": v(-36.58, 5.91) * mm, "end": v(-36.93, 6.18) * mm});
            skArc(sketch, "E74.trimOffspring", {"start": v(-35.43, 4.72) * mm, "mid": v(-35.63, 4.97) * mm, "end": v(-35.84, 5.2) * mm});
            skArc(sketch, "E75.trimOffspring", {"start": v(-34.64, 3.49) * mm, "mid": v(-34.85, 3.88) * mm, "end": v(-35.09, 4.25) * mm});
            skArc(sketch, "E76.trimOffspring", {"start": v(-34.18, 2.37) * mm, "mid": v(-34.28, 2.67) * mm, "end": v(-34.4, 2.96) * mm});
            skArc(sketch, "E77.trimOffspring", {"start": v(-33.86, 0.94) * mm, "mid": v(-33.93, 1.37) * mm, "end": v(-34.02, 1.8) * mm});
            skArc(sketch, "E78.trimOffspring", {"start": v(-33.8, -0.28) * mm, "mid": v(-33.8, 0.04) * mm, "end": v(-33.81, 0.36) * mm});
            skArc(sketch, "E79.trimOffspring", {"start": v(-49.11, -0.94) * mm, "mid": v(-48.91, -1.97) * mm, "end": v(-48.58, -2.96) * mm});
            skArc(sketch, "E80.trimOffspring", {"start": v(-48.33, -3.49) * mm, "mid": v(-48.12, -3.88) * mm, "end": v(-47.89, -4.25) * mm});
            skArc(sketch, "E81.trimOffspring", {"start": v(-47.55, -4.72) * mm, "mid": v(-47.35, -4.97) * mm, "end": v(-47.14, -5.2) * mm});
            skArc(sketch, "E82.trimOffspring", {"start": v(-46.73, -5.62) * mm, "mid": v(-46.4, -5.91) * mm, "end": v(-46.05, -6.18) * mm});
            skArc(sketch, "E83.trimOffspring", {"start": v(-45.57, -6.51) * mm, "mid": v(-45.3, -6.67) * mm, "end": v(-45.01, -6.83) * mm});
            skArc(sketch, "E84.trimOffspring", {"start": v(-44.49, -7.07) * mm, "mid": v(-44.08, -7.23) * mm, "end": v(-43.66, -7.37) * mm});
            skArc(sketch, "E85.trimOffspring", {"start": v(-43.1, -7.51) * mm, "mid": v(-42.78, -7.57) * mm, "end": v(-42.47, -7.62) * mm});
            skArc(sketch, "E86.trimOffspring", {"start": v(-41.89, -7.67) * mm, "mid": v(-41.45, -7.68) * mm, "end": v(-41, -7.67) * mm});
            skArc(sketch, "E87.trimOffspring", {"start": v(-40.43, -7.6) * mm, "mid": v(-40.11, -7.56) * mm, "end": v(-39.8, -7.5) * mm});
            skArc(sketch, "E88.trimOffspring", {"start": v(-39.24, -7.35) * mm, "mid": v(-38.82, -7.2) * mm, "end": v(-38.41, -7.04) * mm});
            skArc(sketch, "E89.trimOffspring", {"start": v(-37.89, -6.79) * mm, "mid": v(-37.61, -6.63) * mm, "end": v(-37.34, -6.47) * mm});
            skArc(sketch, "E90.trimOffspring", {"start": v(-36.86, -6.14) * mm, "mid": v(-36.52, -5.86) * mm, "end": v(-36.19, -5.56) * mm});
            skArc(sketch, "E91.trimOffspring", {"start": v(-35.78, -5.15) * mm, "mid": v(-35.58, -4.9) * mm, "end": v(-35.38, -4.66) * mm});
            skArc(sketch, "E92.trimOffspring", {"start": v(-35.04, -4.18) * mm, "mid": v(-34.81, -3.8) * mm, "end": v(-34.6, -3.42) * mm});
            skArc(sketch, "E93.trimOffspring", {"start": v(-34.37, -2.89) * mm, "mid": v(-34.27, -2.64) * mm, "end": v(-34.18, -2.38) * mm});
            skLineSegment(sketch, "E94", {"start": v(-19.45, -6.88) * mm, "end": v(-34.18, -2.38) * mm});
            skArc(sketch, "E95.trimOffspring", {"start": v(-34, -1.73) * mm, "mid": v(-33.91, -1.3) * mm, "end": v(-33.85, -0.86) * mm});
            skLineSegment(sketch, "E96", {"start": v(-62.22, -16.16) * mm, "end": v(-60.81, -17.81) * mm});
            skLineSegment(sketch, "E97", {"start": v(-65.74, -10.13) * mm, "end": v(-66.5, -8.1) * mm});
            skLineSegment(sketch, "E98", {"start": v(-67.74, -1.22) * mm, "end": v(-67.75, 0.95) * mm});
            skLineSegment(sketch, "E99", {"start": v(-66.57, 7.83) * mm, "end": v(-65.84, 9.87) * mm});
            skLineSegment(sketch, "E100", {"start": v(-37.86, -26.03) * mm, "end": v(-35.73, -25.64) * mm});
            skLineSegment(sketch, "E101", {"start": v(-29.18, -23.22) * mm, "end": v(-27.3, -22.13) * mm});
            skLineSegment(sketch, "E102", {"start": v(-21.98, -17.6) * mm, "end": v(-20.6, -15.94) * mm});
            skLineSegment(sketch, "E103", {"start": v(-46.98, -25.7) * mm, "end": v(-44.84, -26.07) * mm});
            skLineSegment(sketch, "E104", {"start": v(-53.56, -23.35) * mm, "end": v(-55.44, -22.27) * mm});
            skLineSegment(sketch, "E105", {"start": v(-62.38, 15.94) * mm, "end": v(-61, 17.6) * mm});
            skLineSegment(sketch, "E106", {"start": v(-55.67, 22.13) * mm, "end": v(-53.8, 23.22) * mm});
            skLineSegment(sketch, "E107", {"start": v(-47.25, 25.64) * mm, "end": v(-45.11, 26.03) * mm});
            skLineSegment(sketch, "E108", {"start": v(-38.13, 26.07) * mm, "end": v(-36, 25.7) * mm});
            skLineSegment(sketch, "E109", {"start": v(-29.42, 23.35) * mm, "end": v(-27.53, 22.27) * mm});
            skLineSegment(sketch, "E110", {"start": v(-22.16, 17.81) * mm, "end": v(-20.76, 16.16) * mm});
            skLineSegment(sketch, "E111", {"start": v(-17.23, 10.13) * mm, "end": v(-16.48, 8.1) * mm});
            skLineSegment(sketch, "E112", {"start": v(-15.23, 1.22) * mm, "end": v(-15.22, -0.95) * mm});
            skLineSegment(sketch, "E113", {"start": v(-16.4, -7.83) * mm, "end": v(-17.13, -9.87) * mm});
            skLineSegment(sketch, "E114", {"start": v(-49.16, -0.36) * mm, "end": v(-49.17, 0.28) * mm});
            skSolve(sketch);
        }
        {
            var Q0;
            Q0=qSketchRegion(id+"F9",true);
            extrude(context, id + "F10", {"entities" : qUnion([Q0]), "operationType" : NewBodyOperationType.REMOVE, "depth" : 4.5 * mm});
        }
        {
            var Q0;
            Q0=makeQuery(id+"F0.imprint","IMPRINT",FACE,{"disambiguationData":[TD([[makeQuery(id+"F0.imprint","IMPRINT",EDGE,{"derivedFrom":sQuery(id+"F0.wireOp",EDGE,"E0")}),-1.0]])]});
            var sketch = newSketch(context, id + "F11", { "sketchPlane" : qUnion([Q0])});
            skCircle(sketch, "E115", {"center": v(-41.49, 0) * mm, "radius": 5.37 * mm});
            skCircle(sketch, "E116", {"center": v(-41.49, 0) * mm, "radius": 7.09 * mm});
            skLineSegment(sketch, "E117.bottom", {"start": v(-41.49, 0) * mm, "end": v(-41.49, 0) * mm});
            skSolve(sketch);
        }
        {
            var Q0;
            Q0=qSketchRegion(id+"F11",true);
            var Q1;
            Q1=makeQuery(id+"F10.boolean.opBoolean","COPY",FACE,{"derivedFrom":makeQuery(id+"F10.opExtrude","CAP_FACE",FACE,{"disambiguationData":[OSD([sQuery(id+"F9.wireOp",EDGE,"E60.11.3"),sQuery(id+"F9.wireOp",EDGE,"E60.11.4"),sQuery(id+"F9.wireOp",EDGE,"E60.11.5"),sQuery(id+"F9.wireOp",EDGE,"E79.trimOffspring")])],"isStart":false})});
            extrude(context, id + "F12", {"entities" : qUnion([Q0]), "operationType" : NewBodyOperationType.REMOVE, "endBound" : BoundingType.UP_TO_SURFACE, "endBoundEntityFace" : qUnion([Q1]), "depth" : 25 * mm});
        }
        {
            var Q0;
            {var subQ0=sQuery(id+"F0.wireOp",EDGE,"E36");var subQ1=sQuery(id+"F0.wireOp",EDGE,"E35");var subQ2=sQuery(id+"F0.wireOp",EDGE,"E34");var subQ3=sQuery(id+"F0.wireOp",EDGE,"E33");var subQ4=sQuery(id+"F0.wireOp",EDGE,"E32");var subQ5=sQuery(id+"F0.wireOp",EDGE,"E31");var subQ6=sQuery(id+"F0.wireOp",EDGE,"E30");var subQ7=sQuery(id+"F0.wireOp",EDGE,"E29");var subQ8=sQuery(id+"F0.wireOp",EDGE,"E28");var subQ9=sQuery(id+"F0.wireOp",EDGE,"E27");var subQ10=sQuery(id+"F0.wireOp",EDGE,"E26");var subQ11=sQuery(id+"F0.wireOp",EDGE,"E25");var subQ12=sQuery(id+"F0.wireOp",EDGE,"E24");var subQ13=sQuery(id+"F0.wireOp",EDGE,"E23");var subQ14=sQuery(id+"F0.wireOp",EDGE,"E22");var subQ15=sQuery(id+"F0.wireOp",EDGE,"E21");var subQ16=sQuery(id+"F0.wireOp",EDGE,"E20");var subQ17=sQuery(id+"F0.wireOp",EDGE,"E19");var subQ18=sQuery(id+"F0.wireOp",EDGE,"E18");var subQ19=sQuery(id+"F0.wireOp",EDGE,"E17");var subQ20=sQuery(id+"F0.wireOp",EDGE,"E16");var subQ21=sQuery(id+"F0.wireOp",EDGE,"E15");var subQ22=sQuery(id+"F0.wireOp",EDGE,"E14");var subQ23=sQuery(id+"F0.wireOp",EDGE,"E13");var subQ24=sQuery(id+"F0.wireOp",EDGE,"E12");var subQ25=sQuery(id+"F0.wireOp",EDGE,"E11");var subQ26=sQuery(id+"F0.wireOp",EDGE,"E10");var subQ27=sQuery(id+"F0.wireOp",EDGE,"E9");var subQ28=sQuery(id+"F0.wireOp",EDGE,"E8");var subQ29=sQuery(id+"F0.wireOp",EDGE,"E7");var subQ30=sQuery(id+"F0.wireOp",EDGE,"E6");var subQ31=sQuery(id+"F0.wireOp",EDGE,"E5");var subQ32=sQuery(id+"F0.wireOp",EDGE,"E4");var subQ33=sQuery(id+"F0.wireOp",EDGE,"E3");var subQ34=sQuery(id+"F0.wireOp",EDGE,"E1");var subQ35=sQuery(id+"F0.wireOp",EDGE,"E0");Q0=makeQuery(id+"F5.boolean.opBoolean","MERGE",FACE,{"derivedFrom":[makeQuery(id+"F1.opExtrude","CAP_FACE",FACE,{"disambiguationData":[OSD([subQ35,subQ34,subQ33,subQ32,subQ31,subQ30,subQ29,subQ28,subQ27,subQ26,subQ25,subQ24,subQ23,subQ22,subQ21,subQ20,subQ19,subQ18,subQ17,subQ16,subQ15,subQ14,subQ13,subQ12,subQ11,subQ10,subQ9,subQ8,subQ7,subQ6,subQ5,subQ4,subQ3,subQ2,subQ1,subQ0])],"isStart":false}),makeQuery(id+"F5.opExtrude","CAP_FACE",FACE,{"disambiguationData":[OSD([subQ35,subQ34,subQ33,subQ32,subQ31,subQ30,subQ29,subQ28,subQ27,subQ26,subQ25,subQ24,subQ23,subQ22,subQ21,subQ20,subQ19,subQ18,subQ17,subQ16,subQ15,subQ14,subQ13,subQ12,subQ11,subQ10,subQ9,subQ8,subQ7,subQ6,subQ5,subQ4,subQ3,subQ2,subQ1,subQ0])],"isStart":false})]});}
            var sketch = newSketch(context, id + "F13", { "sketchPlane" : qUnion([Q0])});
            skText(sketch, "E118", { "text": "Thomas\nAguirre", "fontName": "OpenSans-Bold.ttf"});
            const initialGuessF13  = {"E118": [-0.0609, 0.00231, 1, 0, 0.00775]};
            skSetInitialGuess(sketch, initialGuessF13);
            skSolve(sketch);
        }
        {
            var Q0;
            Q0=qSketchRegion(id+"F13",true);
            extrude(context, id + "F14", {"entities" : qUnion([Q0]), "operationType" : NewBodyOperationType.ADD, "depth" : 3 * mm});
        }
    });
